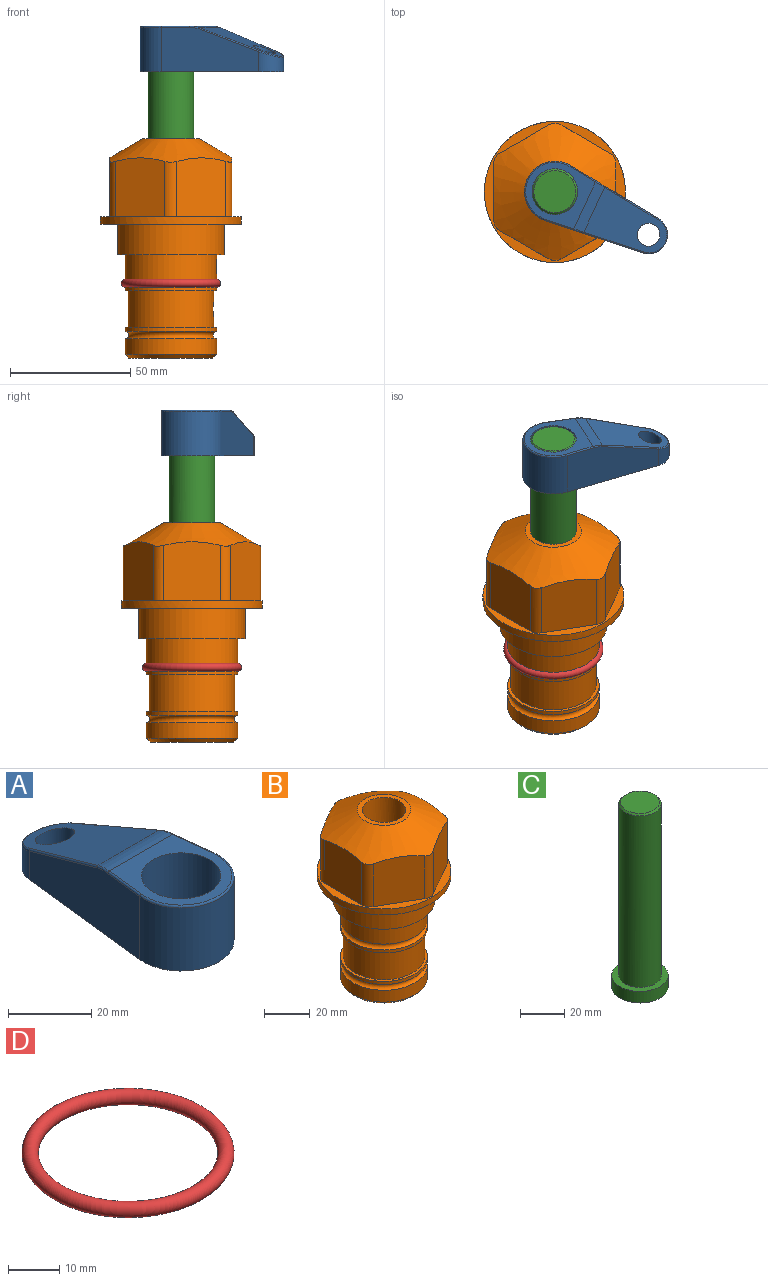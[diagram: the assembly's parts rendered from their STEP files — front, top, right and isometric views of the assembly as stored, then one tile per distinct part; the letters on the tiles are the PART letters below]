
ASSEMBLY  parts=4 mates=2
PART A: 44 faces, bbox 27.5x64.5x19.1 mm
  f0: plane 2.3x0.95mm, normal (0,0,-1), area 1mm2, adj f25,f30,f34
  f1: plane 63.5x25.4mm, normal (0,0,-1), area 561.7mm2, adj f2,f3,f4,f5,f6,f7,f19,f20
  f2: cylinder r=12.7mm len=25.4mm, axis (0,0,-1), area 792.2mm2, adj f1,f3,f5,f13
  f3: plane 42.33x18.54mm, normal (0.99,0.11,0), area 647mm2, adj f1,f2,f4,f11,f12,f14
  f4: cylinder r=7.94mm len=15.78mm, axis (0,0,-1), area 158.6mm2, adj f1,f3,f5,f16
  f5: plane 42.33x18.54mm, normal (-0.99,0.11,0), area 647mm2, adj f1,f2,f4,f15,f17,f18
  f6: cylinder r=9.53mm len=19.05mm, axis (0,0,-1), area 1140.1mm2, adj f1,f8
  f7: cylinder r=4.76mm len=10.98mm, axis (0,0,-1), area 276.1mm2, adj f1,f9
  f8: plane 25.83x24.38mm, normal (0,0,1), area 262.2mm2, adj f6,f10,f11,f13,f15
  f9: plane 32.49x20.55mm, normal (0,0.34,0.94), area 489.9mm2, adj f7,f10,f14,f16,f18
  f10: cylinder r=12.7mm len=21.49mm, axis (-1,0,0), area 93.2mm2, adj f8,f9,f12,f17
  f11: cylinder r=0.51mm len=12.34mm, axis (0.11,-0.99,0), area 9.9mm2, adj f3,f8,f12,f13
  f12: bspline ~7.62x1.64mm, area 3.5mm2, adj f3,f10,f11,f14
  f13: torus R=12.19mm, axis (0,0,1), area 33.6mm2, adj f2,f8,f11,f15
  f14: cylinder r=0.51mm len=26.01mm, axis (0.1,-0.93,0.34), area 21.6mm2, adj f3,f9,f12,f16
  f15: cylinder r=0.51mm len=12.34mm, axis (0.11,0.99,0), area 9.9mm2, adj f5,f8,f13,f17
  f16: bspline ~15.78x7.05mm, area 15.7mm2, adj f4,f9,f14,f18
  f17: bspline ~7.62x1.64mm, area 3.5mm2, adj f5,f10,f15,f18
  f18: cylinder r=0.51mm len=26.01mm, axis (0.1,0.93,-0.34), area 21.6mm2, adj f5,f9,f16,f17
  f19: plane 21.6x14.29mm, normal (-0.99,-0.11,0), area 242.6mm2, adj f1,f26,f28,f34,f36,f38
  f20: plane 21.6x14.29mm, normal (0.99,-0.11,0), area 242.6mm2, adj f1,f27,f29,f37,f39,f41
  f21: cylinder r=12.7mm len=14.29mm, axis (0,0,-1), area 173.2mm2, adj f1,f26,f27,f30,f31,f33
  f22: cylinder r=7.94mm len=7.63mm, axis (0,0,-1), area 53.8mm2, adj f1,f28,f29,f42
  f23: plane 2.3x0.95mm, normal (0,0,-1), area 1mm2, adj f25,f33,f37
  f24: plane 17.94x12.32mm, normal (0,-0.34,-0.94), area 191.2mm2, adj f25,f38,f41,f42
  f25: cylinder r=9.53mm len=12.93mm, axis (-1,0,0), area 37.5mm2, adj f0,f23,f24,f31,f36,f39
  f26: cylinder r=1.59mm len=14.29mm, axis (0,0,-1), area 49mm2, adj f1,f19,f21,f32
  f27: cylinder r=1.59mm len=14.29mm, axis (0,0,-1), area 49mm2, adj f1,f20,f21,f35
  f28: cylinder r=1.59mm len=7.28mm, axis (0,0,-1), area 22.1mm2, adj f1,f19,f22,f40
  f29: cylinder r=1.59mm len=7.28mm, axis (0,0,-1), area 22.1mm2, adj f1,f20,f22,f43
  f30: torus R=14.29mm, axis (0,0,1), area 5.8mm2, adj f0,f21,f31,f32
  f31: bspline ~11.06x2.73mm, area 20.8mm2, adj f21,f25,f30,f33
  f32: sphere r=1.59mm, area 5.4mm2, adj f26,f30,f34
  f33: torus R=14.29mm, axis (0,0,1), area 5.8mm2, adj f21,f23,f31,f35
  f34: cylinder r=1.59mm len=1.68mm, axis (-0.11,0.99,0), area 2.4mm2, adj f0,f19,f32,f36
  f35: sphere r=1.59mm, area 5.4mm2, adj f27,f33,f37
  f36: bspline ~5.82x2.33mm, area 7.7mm2, adj f19,f25,f34,f38
  f37: cylinder r=1.59mm len=1.68mm, axis (0.11,0.99,0), area 2.4mm2, adj f20,f23,f35,f39
  f38: cylinder r=1.59mm len=18.33mm, axis (0.1,-0.93,0.34), area 46.7mm2, adj f19,f24,f36,f40
  f39: bspline ~5.82x2.33mm, area 7.7mm2, adj f20,f25,f37,f41
  f40: sphere r=1.59mm, area 3.6mm2, adj f28,f38,f42
  f41: cylinder r=1.59mm len=18.33mm, axis (0.1,0.93,-0.34), area 46.7mm2, adj f20,f24,f39,f43
  f42: bspline ~8.31x1.84mm, area 15.3mm2, adj f22,f24,f40,f43
  f43: sphere r=1.59mm, area 3.6mm2, adj f29,f41,f42
PART B: 36 faces, bbox 58.7x58.7x91.2 mm
  f0: cylinder r=17.78mm len=35.56mm, axis (0,0,1), area 1670.8mm2, adj f23,f24,f31
  f1: cylinder r=19.05mm len=38.1mm, axis (0,0,1), area 1191.9mm2, adj f26,f27,f30
  f2: plane 58.66x58.66mm, normal (0,0,-1), area 1150.6mm2, adj f3,f28
  f3: cylinder r=29.33mm len=58.66mm, axis (0,0,-1), area 585.1mm2, adj f2,f4
  f4: plane 58.66x58.66mm, normal (0,0,1), area 475.9mm2, adj f3,f5,f6,f7,f8,f9,f10,f11
  f5: plane 24.5x20.32mm, normal (-0.5,0.87,0), area 562.8mm2, adj f4,f15,f16,f17
  f6: plane 24.5x20.32mm, normal (0.5,0.87,0), area 562.8mm2, adj f4,f14,f15,f17
  f7: plane 24.5x23.48mm, normal (1,0,0), area 562.8mm2, adj f4,f13,f14,f17
  f8: plane 24.5x20.32mm, normal (0.5,-0.87,0), area 562.8mm2, adj f4,f12,f13,f17
  f9: plane 24.5x20.32mm, normal (-0.5,-0.87,0), area 562.8mm2, adj f4,f11,f12,f17
  f10: plane 24.5x23.48mm, normal (-1,0,0), area 562.8mm2, adj f4,f11,f16,f17
  f11: cylinder r=5.08mm len=23.01mm, axis (0,0,-1), area 121.2mm2, adj f4,f9,f10,f17
  f12: cylinder r=5.08mm len=23.01mm, axis (0,0,-1), area 121.2mm2, adj f4,f8,f9,f17
  f13: cylinder r=5.08mm len=23.01mm, axis (0,0,-1), area 121.2mm2, adj f4,f7,f8,f17
  f14: cylinder r=5.08mm len=23.01mm, axis (0,0,-1), area 121.2mm2, adj f4,f6,f7,f17
  f15: cylinder r=5.08mm len=23.01mm, axis (0,0,-1), area 121.2mm2, adj f4,f5,f6,f17
  f16: cylinder r=5.08mm len=23.01mm, axis (0,0,-1), area 121.2mm2, adj f4,f5,f10,f17
  f17: cone r=11.73mm half-angle=60deg, axis (0,0,-1), area 2071.8mm2, adj f5,f6,f7,f8,f9,f10,f11,f12
  f18: plane 23.46x23.46mm, normal (0,0,1), area 147.4mm2, adj f17,f35
  f19: plane 34.93x34.93mm, normal (0,0,-1), area 958mm2, adj f29
  f20: cylinder r=19.05mm len=38.1mm, axis (0,0,1), area 760.1mm2, adj f21,f29
  f21: torus R=19.05mm, axis (0,0,1), area 565.3mm2, adj f20,f22
  f22: cylinder r=19.05mm len=38.1mm, axis (0,0,1), area 190mm2, adj f21,f23
  f23: plane 38.1x38.1mm, normal (0,0,1), area 146.9mm2, adj f0,f22
  f24: plane 38.1x38.1mm, normal (0,0,-1), area 146.9mm2, adj f0,f25
  f25: cylinder r=19.05mm len=38.1mm, axis (0,0,1), area 190mm2, adj f24,f26
  f26: torus R=19.05mm, axis (0,0,1), area 565.3mm2, adj f1,f25
  f27: plane 44.45x44.45mm, normal (0,0,-1), area 411.7mm2, adj f1,f28
  f28: cylinder r=22.23mm len=44.45mm, axis (0,0,1), area 1773.5mm2, adj f2,f27
  f29: cone r=19.05mm half-angle=45deg, axis (0,0,1), area 257.5mm2, adj f19,f20
  f30: cylinder r=3.17mm len=6.75mm, axis (-1,0,0), area 128mm2, adj f1,f33
  f31: cylinder r=3.17mm len=6.35mm, axis (-1,0,0), area 102.5mm2, adj f0,f33
  f32: plane 25.4x25.4mm, normal (0,0,1), area 506.7mm2, adj f33
  f33: cylinder r=12.7mm len=66.42mm, axis (0,0,-1), area 5236.2mm2, adj f30,f31,f32,f34
  f34: cone r=9.53mm half-angle=30deg, axis (0,0,-1), area 443.4mm2, adj f33,f35
  f35: cylinder r=9.53mm len=19.05mm, axis (0,0,-1), area 849mm2, adj f18,f34
PART C: 6 faces, bbox 25.4x25.4x101.6 mm
  f0: plane 17.46x17.46mm, normal (0,0,1), area 239.5mm2, adj f5
  f1: plane 25.4x25.4mm, normal (0,0,-1), area 506.7mm2, adj f2
  f2: cylinder r=12.7mm len=25.4mm, axis (0,0,1), area 506.7mm2, adj f1,f3
  f3: plane 25.4x25.4mm, normal (0,0,1), area 221.7mm2, adj f2,f4
  f4: cylinder r=9.53mm len=94.46mm, axis (0,0,1), area 5653mm2, adj f3,f5
  f5: cone r=8.73mm half-angle=45deg, axis (0,0,-1), area 64.4mm2, adj f0,f4
PART D: 1 faces, bbox 44.7x44.7x3.2 mm
  f0: torus R=19.05mm, axis (0,0,1), area 1193.9mm2
PLACE A rot(axis=(0,0,-1),114.7deg) t=(0,0,63.43)mm
PLACE B at identity fixed
PLACE C rot(axis=(0,0,-1),24.7deg) t=(0,0,8.82)mm
PLACE D at identity
MATE cylindrical C.f2 <-> B.f0  axis (0,0,1) through (0,0,34.46)mm
MATE fastened A.f2 <-> C.f2  axis (0,0,-1) through (0,0,82.48)mm
